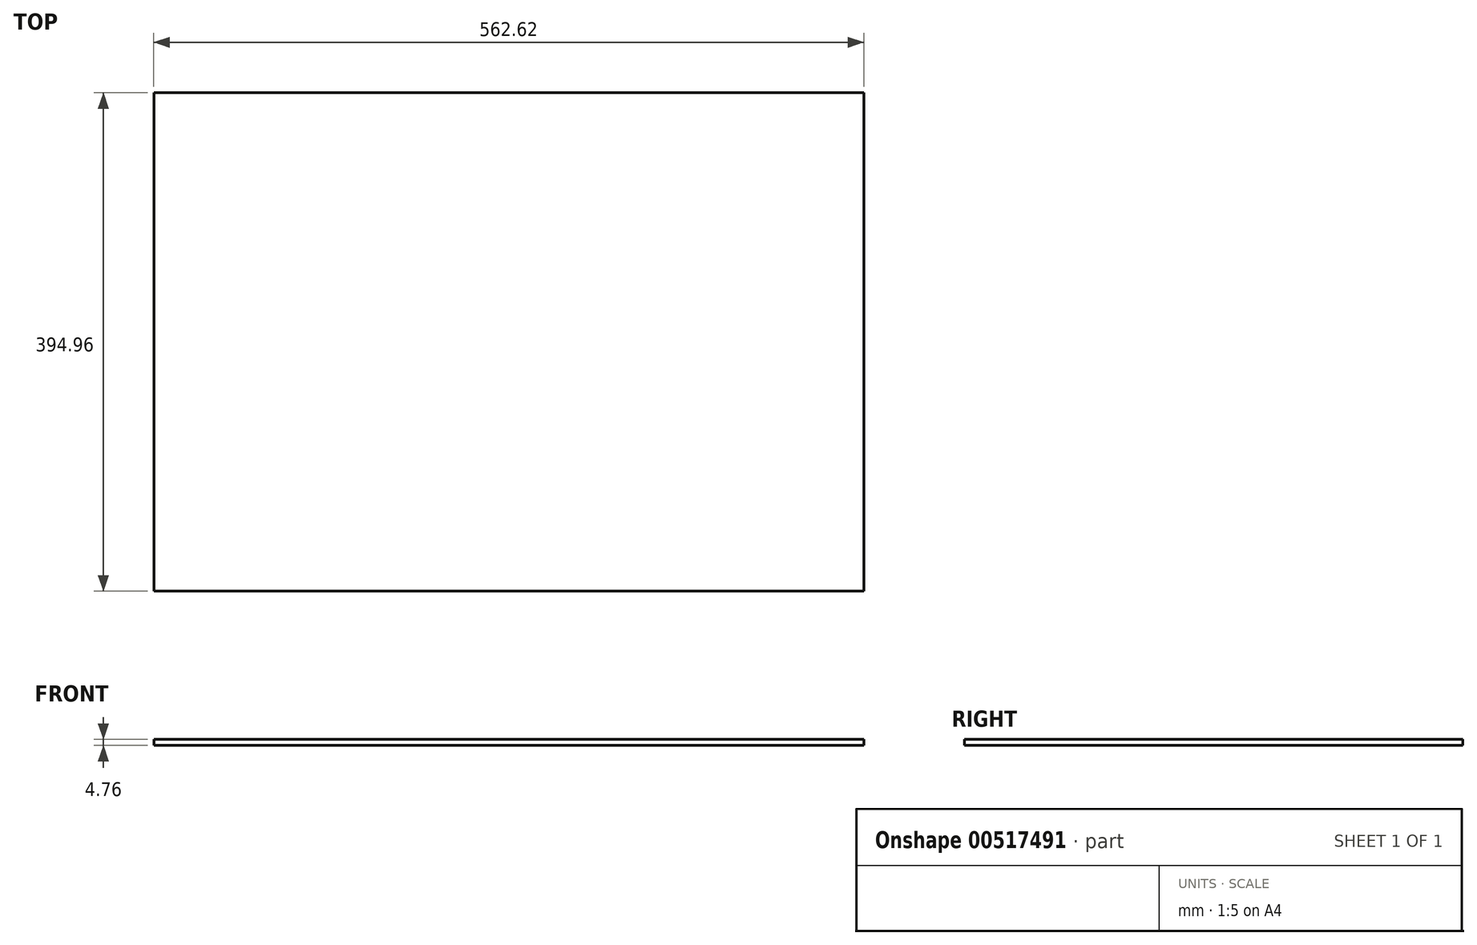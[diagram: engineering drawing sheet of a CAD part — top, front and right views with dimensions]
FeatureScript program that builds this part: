
annotation { "Feature Type Name" : "Feature", "Feature Type Description" : "" }
export const myFeature = defineFeature(function(context is Context, id is Id, definition is map)
    precondition{}
    {
        {
            var Q0;
            Q0=qCreatedBy(makeId("Top.planeOp"),FACE);
            var sketch = newSketch(context, id + "F0", { "sketchPlane" : qUnion([Q0])});
            skLineSegment(sketch, "E0.bottom", {"start": v(281.3, -197.48) * mm, "end": v(-281.3, -197.49) * mm});
            skLineSegment(sketch, "E0.top", {"start": v(281.3, 197.49) * mm, "end": v(-281.3, 197.48) * mm});
            skLineSegment(sketch, "E0.left", {"start": v(281.3, -197.48) * mm, "end": v(281.3, 197.49) * mm});
            skLineSegment(sketch, "E0.right", {"start": v(-281.3, -197.49) * mm, "end": v(-281.3, 197.48) * mm});
            skPoint(sketch, "E0.middle", {"position": v(0, 0) * mm});
            skSolve(sketch);
        }
        {
            var Q0;
            Q0=makeQuery(id+"F0.imprint","IMPRINT",FACE,{"disambiguationData":[TD([[makeQuery(id+"F0.imprint","IMPRINT",EDGE,{"derivedFrom":sQuery(id+"F0.wireOp",EDGE,"E0.bottom")}),-1.0]])]});
            extrude(context, id + "F1", {"entities" : qUnion([Q0]), "depth" : 4.76 * mm, "offsetDistance" : 25.4 * mm});
        }
    });
